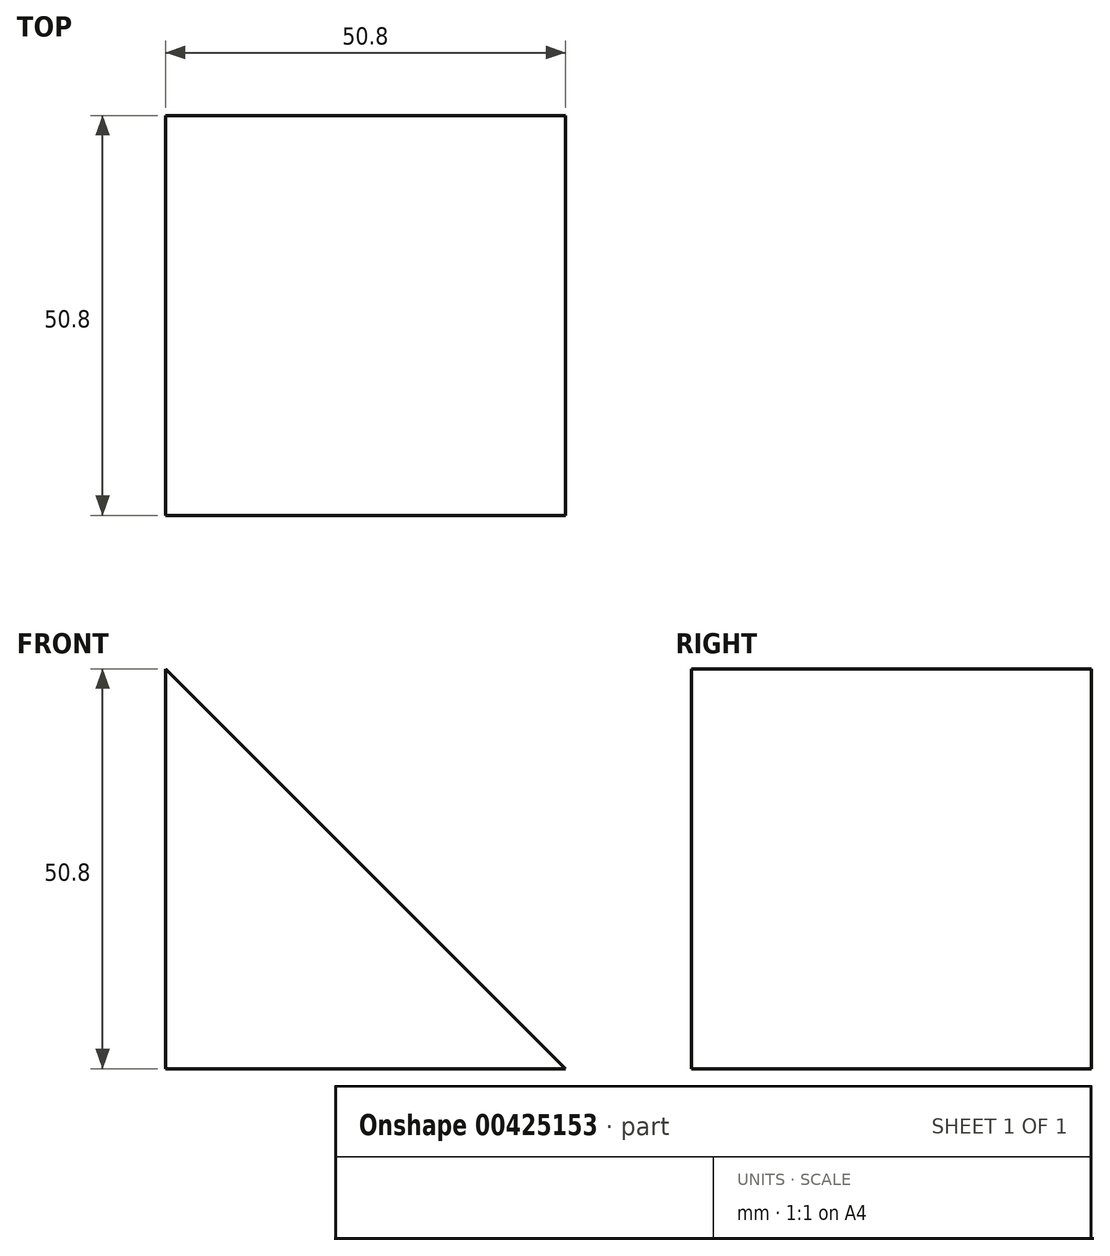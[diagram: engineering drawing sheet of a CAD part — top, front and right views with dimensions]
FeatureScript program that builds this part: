
annotation { "Feature Type Name" : "Feature", "Feature Type Description" : "" }
export const myFeature = defineFeature(function(context is Context, id is Id, definition is map)
    precondition{}
    {
        {
            var Q0;
            Q0=qCreatedBy(makeId("Front.planeOp"),FACE);
            var sketch = newSketch(context, id + "F0", { "sketchPlane" : qUnion([Q0])});
            skLineSegment(sketch, "E0", {"start": v(-36.28, 40.1) * mm, "end": v(-36.28, -10.7) * mm});
            skLineSegment(sketch, "E1", {"start": v(-36.28, -10.7) * mm, "end": v(14.52, -10.7) * mm});
            skLineSegment(sketch, "E2", {"start": v(14.52, -10.7) * mm, "end": v(-36.28, 40.1) * mm});
            skSolve(sketch);
        }
        {
            var Q0;
            Q0 = qSketchRegion(id + "F0", true);
            extrude(context, id + "F1", {"entities" : qUnion([Q0]), "depth" : 50.8 * mm});
        }
    });
